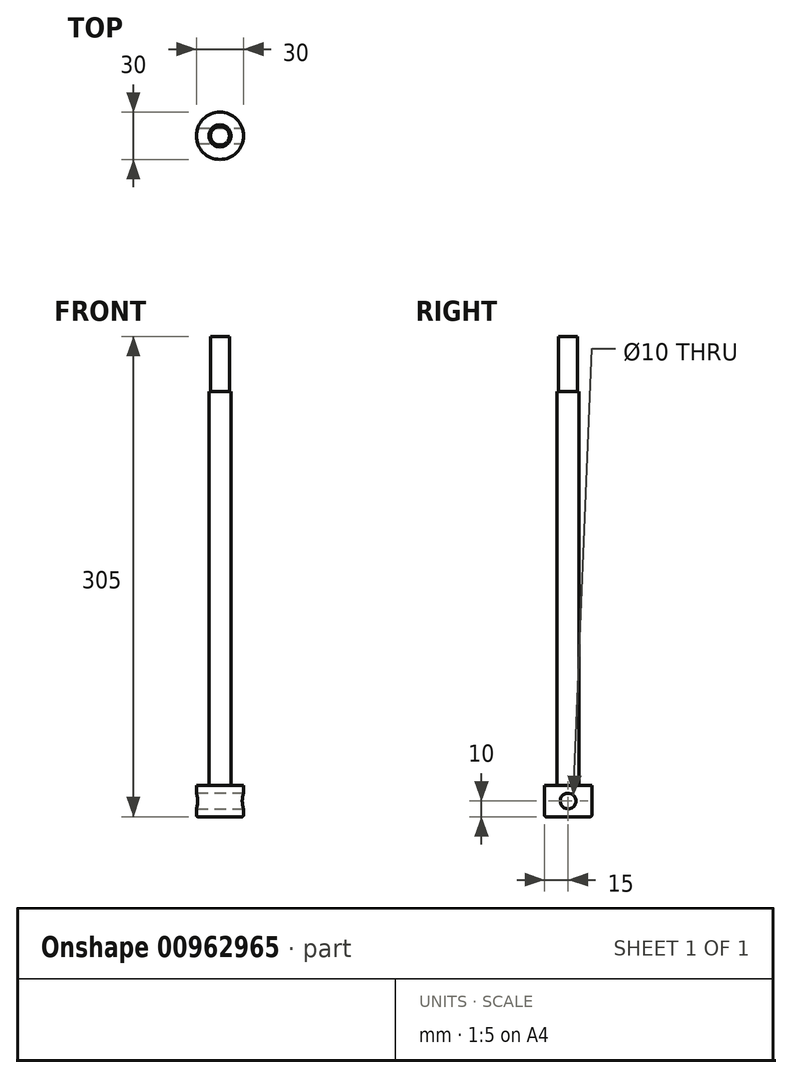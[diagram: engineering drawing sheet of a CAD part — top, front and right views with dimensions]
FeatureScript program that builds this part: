
annotation { "Feature Type Name" : "Feature", "Feature Type Description" : "" }
export const myFeature = defineFeature(function(context is Context, id is Id, definition is map)
    precondition{}
    {
        {
            var Q0;
            Q0=qCreatedBy(makeId("Top.planeOp"),FACE);
            var sketch = newSketch(context, id + "F0", { "sketchPlane" : qUnion([Q0])});
            skCircle(sketch, "E0", {"center": v(0, 0) * mm, "radius": 7 * mm});
            skSolve(sketch);
        }
        {
            var Q0;
            Q0 = qSketchRegion(id + "F0", true);
            extrude(context, id + "F1", {"entities" : qUnion([Q0]), "depth" : 250 * mm, "offsetDistance" : 25 * mm, "symmetric" : true});
        }
        {
            var Q0;
            Q0=makeQuery(id+"F1.opExtrude","CAP_FACE",FACE,{"disambiguationData":[OSD([sQuery(id+"F0.wireOp",EDGE,"E0")])],"isStart":false});
            var sketch = newSketch(context, id + "F2", { "sketchPlane" : qUnion([Q0])});
            skCircle(sketch, "E1", {"center": v(0, 0) * mm, "radius": 6 * mm});
            skSolve(sketch);
        }
        {
            var Q0;
            Q0 = qSketchRegion(id + "F2", true);
            extrude(context, id + "F3", {"entities" : qUnion([Q0]), "operationType" : NewBodyOperationType.ADD, "depth" : 35 * mm, "offsetDistance" : 25 * mm});
        }
        {
            var Q0;
            Q0=makeQuery(id+"F1.opExtrude","CAP_FACE",FACE,{"disambiguationData":[OSD([sQuery(id+"F0.wireOp",EDGE,"E0")])],"isStart":true});
            var sketch = newSketch(context, id + "F4", { "sketchPlane" : qUnion([Q0])});
            skCircle(sketch, "E2", {"center": v(0, 0) * mm, "radius": 15 * mm});
            skSolve(sketch);
        }
        {
            var Q0;
            Q0 = qSketchRegion(id + "F4", true);
            extrude(context, id + "F5", {"entities" : qUnion([Q0]), "operationType" : NewBodyOperationType.ADD, "depth" : 20 * mm, "offsetDistance" : 25 * mm});
        }
        {
            var Q0;
            Q0=qCreatedBy(makeId("Right.planeOp"),FACE);
            var sketch = newSketch(context, id + "F6", { "sketchPlane" : qUnion([Q0])});
            skCircle(sketch, "E3", {"center": v(0, -135) * mm, "radius": 5 * mm});
            skSolve(sketch);
        }
        {
            var Q0;
            Q0 = qSketchRegion(id + "F6", true);
            extrude(context, id + "F7", {"entities" : qUnion([Q0]), "operationType" : NewBodyOperationType.REMOVE, "endBound" : BoundingType.THROUGH_ALL, "oppositeDirection" : true, "depth" : 25 * mm, "offsetDistance" : 25 * mm, "hasSecondDirection" : true, "secondDirectionOppositeDirection" : false, "secondDirectionDepth" : 25 * mm});
        }
        {
            var Q0;
            Q0=makeQuery(id+"F5.opExtrude","CAP_EDGE",EDGE,{"disambiguationData":[OSD([sQuery(id+"F4.wireOp",EDGE,"E2")])],"isStart":false});
            fillet(context, id + "F8", {"entities" : qUnion([Q0]), "radius" : 1 * mm, "tangentPropagation" : true, "allowEdgeOverflow" : false});
        }
    });
